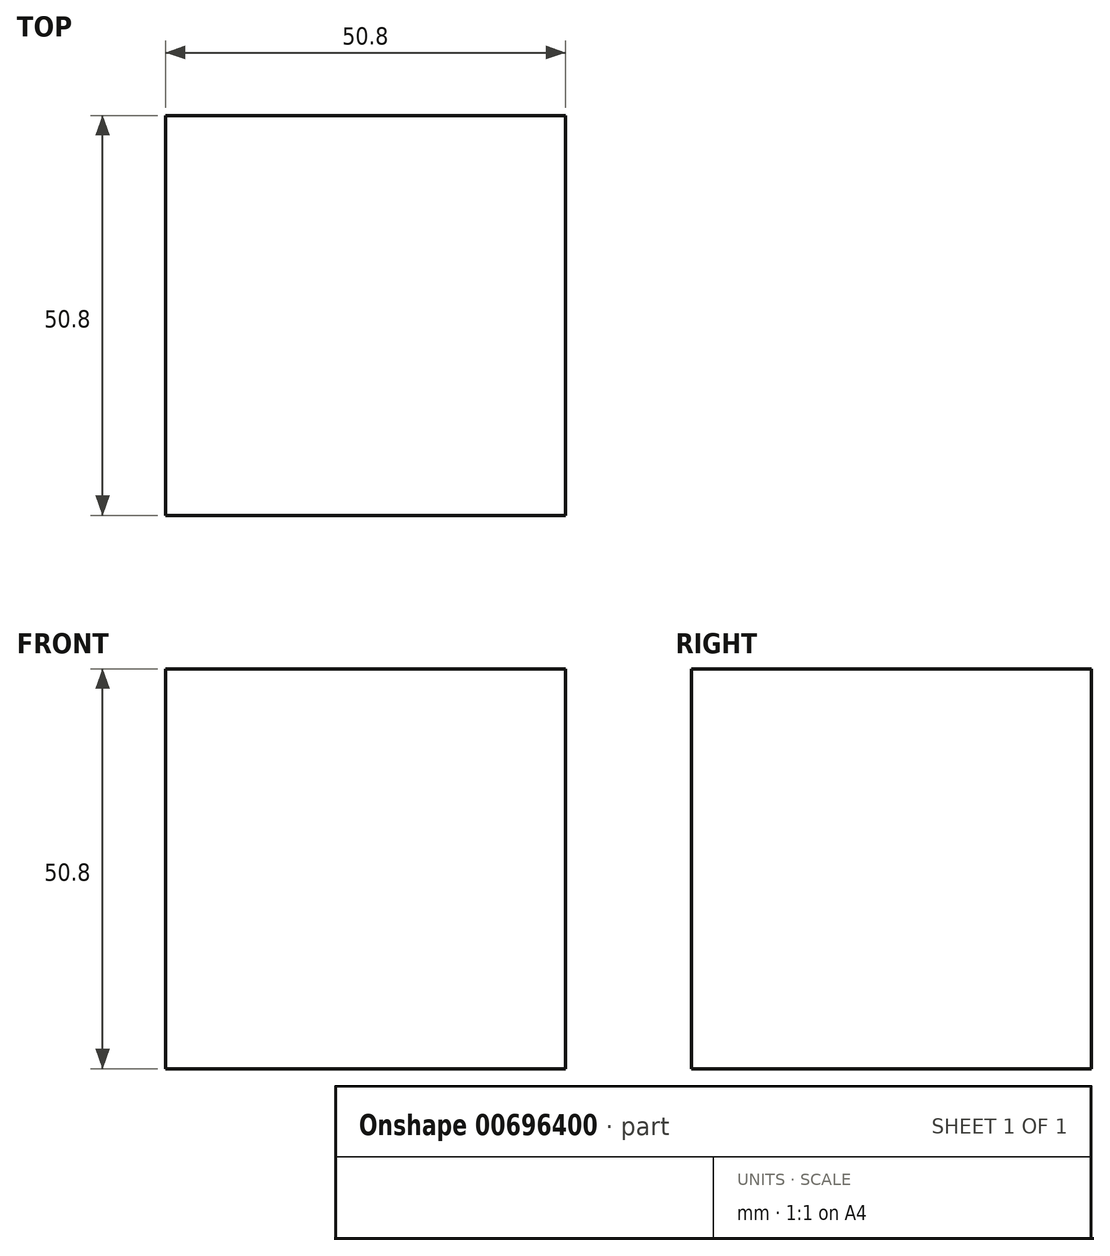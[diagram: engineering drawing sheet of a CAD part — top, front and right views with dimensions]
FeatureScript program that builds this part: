
annotation { "Feature Type Name" : "Feature", "Feature Type Description" : "" }
export const myFeature = defineFeature(function(context is Context, id is Id, definition is map)
    precondition{}
    {
        {
            var Q0;
            Q0=qCreatedBy(makeId("Front.planeOp"),FACE);
            var sketch = newSketch(context, id + "F0", { "sketchPlane" : qUnion([Q0])});
            skLineSegment(sketch, "E0.bottom", {"start": v(0, 0) * mm, "end": v(-50.8, 0) * mm});
            skLineSegment(sketch, "E0.top", {"start": v(0, 50.8) * mm, "end": v(-50.8, 50.8) * mm});
            skLineSegment(sketch, "E0.left", {"start": v(0, 0) * mm, "end": v(0, 50.8) * mm});
            skLineSegment(sketch, "E0.right", {"start": v(-50.8, 0) * mm, "end": v(-50.8, 50.8) * mm});
            skSolve(sketch);
        }
        {
            var Q0;
            Q0=makeQuery(id+"F0.imprint","IMPRINT",FACE,{"disambiguationData":[TD([[makeQuery(id+"F0.imprint","IMPRINT",EDGE,{"derivedFrom":sQuery(id+"F0.wireOp",EDGE,"E0.bottom")}),-1.0]])]});
            extrude(context, id + "F1", {"entities" : qUnion([Q0]), "depth" : 50.8 * mm, "offsetDistance" : 25.4 * mm});
        }
        {
            var Q0;
            Q0=qCreatedBy(makeId("Front.planeOp"),FACE);
            var sketch = newSketch(context, id + "F2", { "sketchPlane" : qUnion([Q0])});
            skLineSegment(sketch, "E1.bottom", {"start": v(0, 50.9) * mm, "end": v(-25.4, 50.9) * mm});
            skLineSegment(sketch, "E1.top", {"start": v(0, 25.4) * mm, "end": v(-25.4, 25.4) * mm});
            skLineSegment(sketch, "E1.left", {"start": v(0, 50.9) * mm, "end": v(0, 25.4) * mm});
            skLineSegment(sketch, "E1.right", {"start": v(-25.4, 50.9) * mm, "end": v(-25.4, 25.4) * mm});
            skSolve(sketch);
        }
        {
            var Q0;
            Q0=makeQuery(id+"F2.imprint","IMPRINT",FACE,{"disambiguationData":[TD([[makeQuery(id+"F2.imprint","IMPRINT",EDGE,{"derivedFrom":sQuery(id+"F2.wireOp",EDGE,"E1.bottom")}),1.0]])]});
            extrude(context, id + "F3", {"entities" : qUnion([Q0]), "operationType" : NewBodyOperationType.REMOVE, "oppositeDirection" : true, "depth" : 25.4 * mm, "offsetDistance" : 25.4 * mm});
        }
    });
